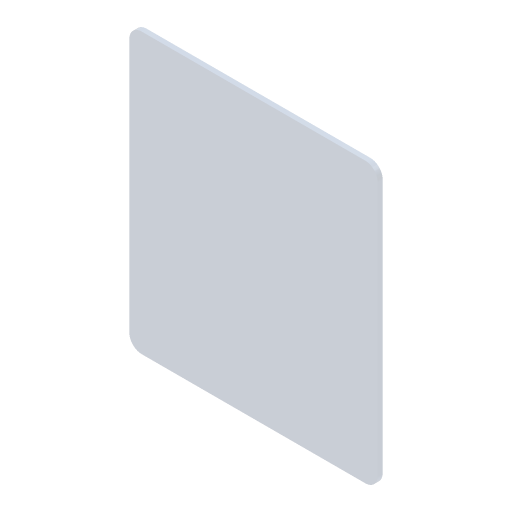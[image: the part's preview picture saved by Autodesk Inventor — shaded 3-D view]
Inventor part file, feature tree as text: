
AUTODESK INVENTOR PART (.ipt)
format: ipt  version: 2024.1 (Build 281209000, 209)  size: 90,112 bytes
history: native  units: mm
features: extrude x1, sketch x1
ambient origin geometry x8: Origin, YZ Plane, XZ Plane, XY Plane, X Axis, Y Axis, Z Axis, Center Point
bodies: Solid1 (feature_tree)
feature tree (2):
  extrude  "Extrusion1"  Depth=450.0mm
  sketch  "Sketch1"  dims[d0=400.0mm d1=450.0mm d2=20.0mm d3=8.0mm d4=0.0mm]
